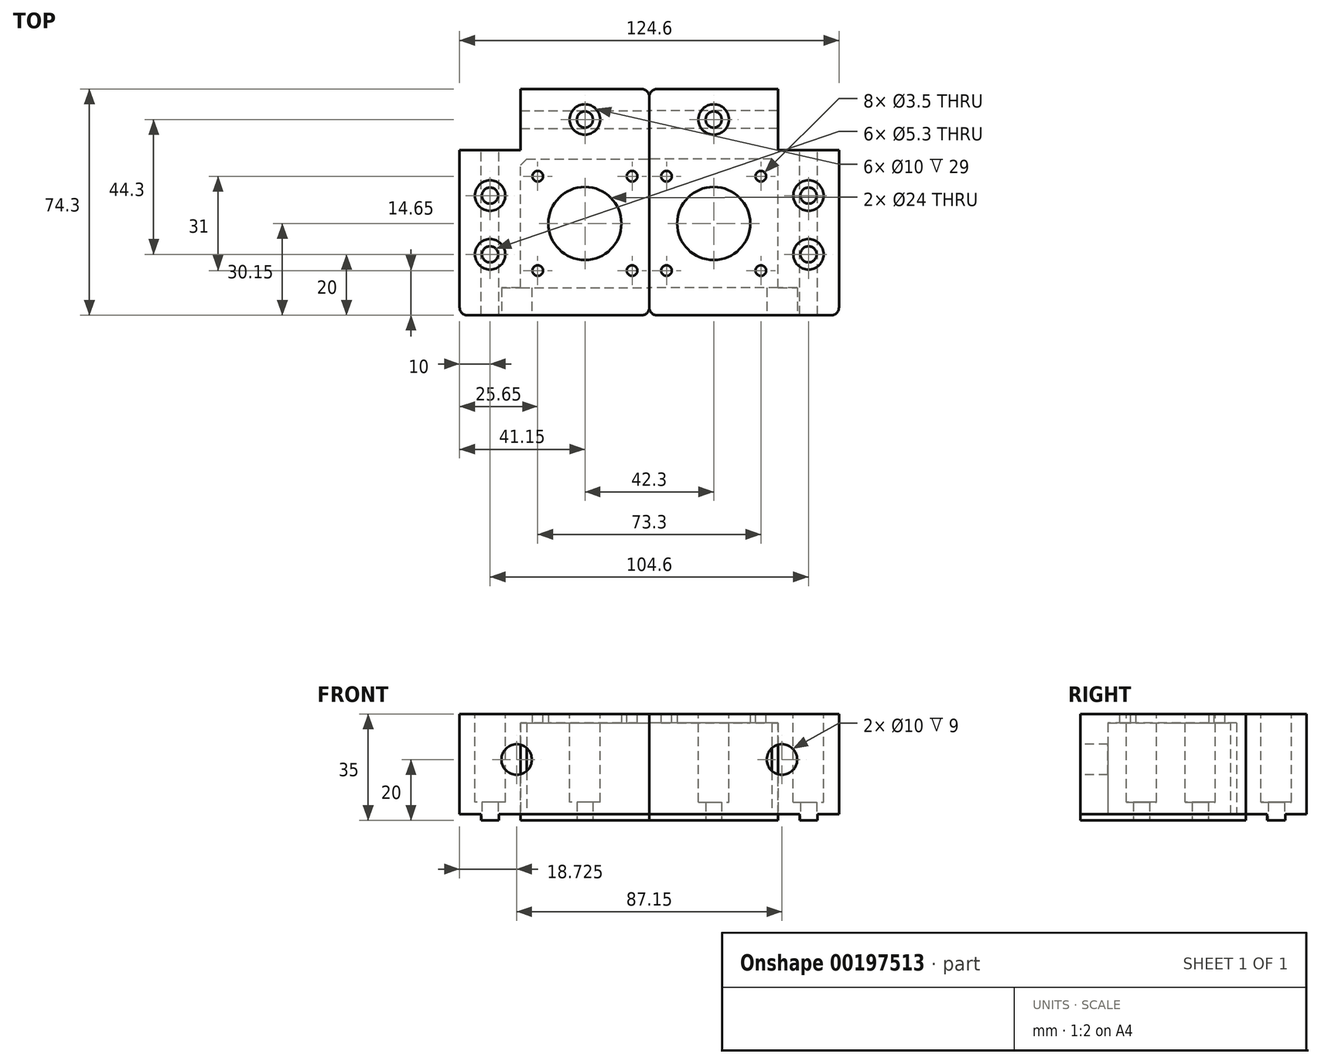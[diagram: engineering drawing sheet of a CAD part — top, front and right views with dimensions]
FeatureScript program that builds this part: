
annotation { "Feature Type Name" : "Feature", "Feature Type Description" : "" }
export const myFeature = defineFeature(function(context is Context, id is Id, definition is map)
    precondition{}
    {
        {
            var Q0;
            Q0=qCreatedBy(makeId("Top.planeOp"),FACE);
            var sketch = newSketch(context, id + "F0", { "sketchPlane" : qUnion([Q0])});
            skLineSegment(sketch, "E0", {"start": v(-21.15, 44.15) * mm, "end": v(21.15, 44.15) * mm});
            skCircle(sketch, "E1", {"center": v(0, 0) * mm, "radius": 12 * mm});
            skCircle(sketch, "E2", {"center": v(-31.15, 9.15) * mm, "radius": 2.65 * mm});
            skCircle(sketch, "E3", {"center": v(0, 34.15) * mm, "radius": 2.65 * mm});
            skPoint(sketch, "E3.centerSnap0", {"position": v(0, 44.15) * mm});
            skPoint(sketch, "E3.centerSnap1", {"position": v(-21.15, 34.15) * mm});
            skLineSegment(sketch, "E4.left", {"start": v(-41.15, 24.15) * mm, "end": v(-41.15, -30.15) * mm});
            skLineSegment(sketch, "E4.right", {"start": v(21.15, 44.15) * mm, "end": v(21.15, -30.15) * mm});
            skCircle(sketch, "E5", {"center": v(-31.15, -10.15) * mm, "radius": 2.65 * mm});
            skLineSegment(sketch, "E6", {"start": v(-41.15, -30.15) * mm, "end": v(21.15, -30.15) * mm});
            skPoint(sketch, "E7.orphan", {"position": v(21.15, 24.15) * mm});
            skLineSegment(sketch, "E8", {"start": v(-41.15, 24.15) * mm, "end": v(-21.15, 24.15) * mm});
            skLineSegment(sketch, "E9", {"start": v(-21.15, 24.15) * mm, "end": v(-21.15, 44.15) * mm});
            skSolve(sketch);
        }
        {
            var Q0;
            Q0=qSketchRegion(id+"F0",true);
            extrude(context, id + "F1", {"entities" : qUnion([Q0]), "depth" : 33 * mm});
        }
        {
            var Q0;
            Q0=makeQuery(id+"F1.opExtrude","SWEPT_FACE",FACE,{"disambiguationData":[OSD([sQuery(id+"F0.wireOp",EDGE,"E6")])]});
            var sketch = newSketch(context, id + "F2", { "sketchPlane" : qUnion([Q0])});
            skCircle(sketch, "E10", {"center": v(-22.43, 18) * mm, "radius": 5 * mm});
            skSolve(sketch);
        }
        {
            var Q0;
            Q0=qSketchRegion(id+"F2",true);
            extrude(context, id + "F3", {"entities" : qUnion([Q0]), "operationType" : NewBodyOperationType.REMOVE, "oppositeDirection" : true, "depth" : 9 * mm});
        }
        {
            var Q0;
            Q0=makeQuery(id+"F0.imprint","IMPRINT",FACE,{"disambiguationData":[TD([[makeQuery(id+"F0.imprint","IMPRINT",EDGE,{"derivedFrom":sQuery(id+"F0.wireOp",EDGE,"E0")}),-1.0]])]});
            var sketch = newSketch(context, id + "F4", { "sketchPlane" : qUnion([Q0])});
            skLineSegment(sketch, "E11.bottom", {"start": v(-21.15, -21.15) * mm, "end": v(21.15, -21.15) * mm});
            skLineSegment(sketch, "E11.top", {"start": v(-21.15, 21.15) * mm, "end": v(21.15, 21.15) * mm});
            skLineSegment(sketch, "E11.left", {"start": v(-21.15, -21.15) * mm, "end": v(-21.15, 21.15) * mm});
            skLineSegment(sketch, "E11.right", {"start": v(21.15, -21.15) * mm, "end": v(21.15, 21.15) * mm});
            skSolve(sketch);
        }
        {
            var Q0;
            Q0=qSketchRegion(id+"F4",true);
            extrude(context, id + "F5", {"entities" : qUnion([Q0]), "operationType" : NewBodyOperationType.REMOVE, "depth" : 30 * mm});
        }
        {
            var Q0;
            Q0=makeQuery(id+"F5.boolean.opBoolean","COPY",EDGE,{"derivedFrom":makeQuery(id+"F5.opExtrude","SWEPT_EDGE",EDGE,{"disambiguationData":[OSD([sQuery(id+"F4.wireOp",EDGE,"E11.top"),sQuery(id+"F4.wireOp",EDGE,"E11.left")])]})});
            chamfer(context, id + "F6", {"entities" : qUnion([Q0]), "width" : 2 * mm, "tangentPropagation" : true});
        }
        {
            var Q0;
            Q0=makeQuery(id+"F1.opExtrude","SWEPT_EDGE",EDGE,{"disambiguationData":[OSD([sQuery(id+"F0.wireOp",EDGE,"E4.left"),sQuery(id+"F0.wireOp",EDGE,"E6")])]});
            var Q1;
            Q1=makeQuery(id+"F1.opExtrude","SWEPT_EDGE",EDGE,{"disambiguationData":[OSD([sQuery(id+"F0.wireOp",EDGE,"E4.right"),sQuery(id+"F0.wireOp",EDGE,"E6")])]});
            var Q2;
            Q2=makeQuery(id+"F1.opExtrude","SWEPT_EDGE",EDGE,{"disambiguationData":[OSD([sQuery(id+"F0.wireOp",EDGE,"E0"),sQuery(id+"F0.wireOp",EDGE,"E4.right")])]});
            fillet(context, id + "F7", {"entities" : qUnion([Q0, Q1, Q2]), "radius" : 2.5 * mm, "tangentPropagation" : true, "allowEdgeOverflow" : false});
        }
        {
            var Q0;
            Q0=makeQuery(id+"F1.opExtrude","CAP_FACE",FACE,{"disambiguationData":[OSD([sQuery(id+"F0.wireOp",EDGE,"E0"),sQuery(id+"F0.wireOp",EDGE,"E1"),sQuery(id+"F0.wireOp",EDGE,"E2"),sQuery(id+"F0.wireOp",EDGE,"E3"),sQuery(id+"F0.wireOp",EDGE,"E4.left"),sQuery(id+"F0.wireOp",EDGE,"E4.right"),sQuery(id+"F0.wireOp",EDGE,"E5"),sQuery(id+"F0.wireOp",EDGE,"E6"),sQuery(id+"F0.wireOp",EDGE,"E8"),sQuery(id+"F0.wireOp",EDGE,"E9")])],"isStart":false});
            var sketch = newSketch(context, id + "F8", { "sketchPlane" : qUnion([Q0])});
            skPoint(sketch, "E12.0", {"position": v(0, 34.15) * mm});
            skPoint(sketch, "E12.1", {"position": v(-31.15, 9.15) * mm});
            skPoint(sketch, "E12.2", {"position": v(-31.15, -10.15) * mm});
            skCircle(sketch, "E13", {"center": v(0, 34.15) * mm, "radius": 5 * mm});
            skCircle(sketch, "E14", {"center": v(-31.15, 9.15) * mm, "radius": 5 * mm});
            skCircle(sketch, "E15", {"center": v(-31.15, -10.15) * mm, "radius": 5 * mm});
            skSolve(sketch);
        }
        {
            var Q0;
            Q0=qSketchRegion(id+"F8",true);
            extrude(context, id + "F9", {"entities" : qUnion([Q0]), "operationType" : NewBodyOperationType.REMOVE, "oppositeDirection" : true, "depth" : 29 * mm});
        }
        {
            var Q0;
            Q0=makeQuery(id+"F0.imprint","IMPRINT",FACE,{"disambiguationData":[TD([[makeQuery(id+"F0.imprint","IMPRINT",EDGE,{"derivedFrom":sQuery(id+"F0.wireOp",EDGE,"E0")}),-1.0]])]});
            var sketch = newSketch(context, id + "F10", { "sketchPlane" : qUnion([Q0])});
            skLineSegment(sketch, "E16.bottom", {"start": v(-34.1, -30.15) * mm, "end": v(-28.2, -30.15) * mm});
            skLineSegment(sketch, "E16.top", {"start": v(-34.1, 24.15) * mm, "end": v(-28.2, 24.15) * mm});
            skLineSegment(sketch, "E16.left", {"start": v(-34.1, -30.15) * mm, "end": v(-34.1, 24.15) * mm});
            skLineSegment(sketch, "E16.right", {"start": v(-28.2, -30.15) * mm, "end": v(-28.2, 24.15) * mm});
            skLineSegment(sketch, "E17.bottom", {"start": v(-21.15, 31.2) * mm, "end": v(21.15, 31.2) * mm});
            skLineSegment(sketch, "E17.top", {"start": v(-21.15, 37.1) * mm, "end": v(21.15, 37.1) * mm});
            skLineSegment(sketch, "E17.left", {"start": v(-21.15, 31.2) * mm, "end": v(-21.15, 37.1) * mm});
            skLineSegment(sketch, "E17.right", {"start": v(21.15, 31.2) * mm, "end": v(21.15, 37.1) * mm});
            skCircle(sketch, "E18.0", {"center": v(-31.15, -10.15) * mm, "radius": 2.65 * mm});
            skCircle(sketch, "E19.0", {"center": v(-31.15, 9.15) * mm, "radius": 2.65 * mm});
            skCircle(sketch, "E20.0", {"center": v(0, 34.15) * mm, "radius": 2.65 * mm});
            skSolve(sketch);
        }
        {
            var Q0;
            Q0=qSketchRegion(id+"F10",true);
            extrude(context, id + "F11", {"entities" : qUnion([Q0]), "operationType" : NewBodyOperationType.ADD, "oppositeDirection" : true, "depth" : 2 * mm});
        }
        {
            var Q0;
            Q0=makeQuery(id+"F1.opExtrude","CAP_FACE",FACE,{"disambiguationData":[OSD([sQuery(id+"F0.wireOp",EDGE,"E0"),sQuery(id+"F0.wireOp",EDGE,"E1"),sQuery(id+"F0.wireOp",EDGE,"E2"),sQuery(id+"F0.wireOp",EDGE,"E3"),sQuery(id+"F0.wireOp",EDGE,"E4.left"),sQuery(id+"F0.wireOp",EDGE,"E4.right"),sQuery(id+"F0.wireOp",EDGE,"E5"),sQuery(id+"F0.wireOp",EDGE,"E6"),sQuery(id+"F0.wireOp",EDGE,"E8"),sQuery(id+"F0.wireOp",EDGE,"E9")])],"isStart":false});
            var sketch = newSketch(context, id + "F12", { "sketchPlane" : qUnion([Q0])});
            skLineSegment(sketch, "E21.bottom", {"start": v(-15.5, 15.5) * mm, "end": v(15.5, 15.5) * mm, "construction": true});
            skLineSegment(sketch, "E21.top", {"start": v(-15.5, -15.5) * mm, "end": v(15.5, -15.5) * mm, "construction": true});
            skLineSegment(sketch, "E21.left", {"start": v(-15.5, 15.5) * mm, "end": v(-15.5, -15.5) * mm, "construction": true});
            skLineSegment(sketch, "E21.right", {"start": v(15.5, 15.5) * mm, "end": v(15.5, -15.5) * mm, "construction": true});
            skCircle(sketch, "E22", {"center": v(15.5, 15.5) * mm, "radius": 1.75 * mm});
            skCircle(sketch, "E23", {"center": v(15.5, -15.5) * mm, "radius": 1.75 * mm});
            skCircle(sketch, "E24", {"center": v(-15.5, -15.5) * mm, "radius": 1.75 * mm});
            skCircle(sketch, "E25", {"center": v(-15.5, 15.5) * mm, "radius": 1.75 * mm});
            skSolve(sketch);
        }
        {
            var Q0;
            Q0=qSketchRegion(id+"F12",true);
            extrude(context, id + "F13", {"entities" : qUnion([Q0]), "operationType" : NewBodyOperationType.REMOVE, "endBound" : BoundingType.THROUGH_ALL, "oppositeDirection" : true, "depth" : 25 * mm});
        }
        {
            var Q0;
            Q0=makeQuery(id+"F1.opExtrude","SWEPT_BODY",BODY,{"disambiguationData":[OSD([sQuery(id+"F0.wireOp",EDGE,"E0"),sQuery(id+"F0.wireOp",EDGE,"E1"),sQuery(id+"F0.wireOp",EDGE,"E2"),sQuery(id+"F0.wireOp",EDGE,"E3"),sQuery(id+"F0.wireOp",EDGE,"E4.left"),sQuery(id+"F0.wireOp",EDGE,"E4.right"),sQuery(id+"F0.wireOp",EDGE,"E5"),sQuery(id+"F0.wireOp",EDGE,"E6"),sQuery(id+"F0.wireOp",EDGE,"E8"),sQuery(id+"F0.wireOp",EDGE,"E9")])]});
            var Q1;
            Q1=makeQuery(id+"F1.opExtrude","SWEPT_FACE",FACE,{"disambiguationData":[OSD([sQuery(id+"F0.wireOp",EDGE,"E4.right")])]});
            mirror(context, id + "F14", {"entities" : qUnion([Q0]), "mirrorPlane" : qUnion([Q1])});
        }
    });
